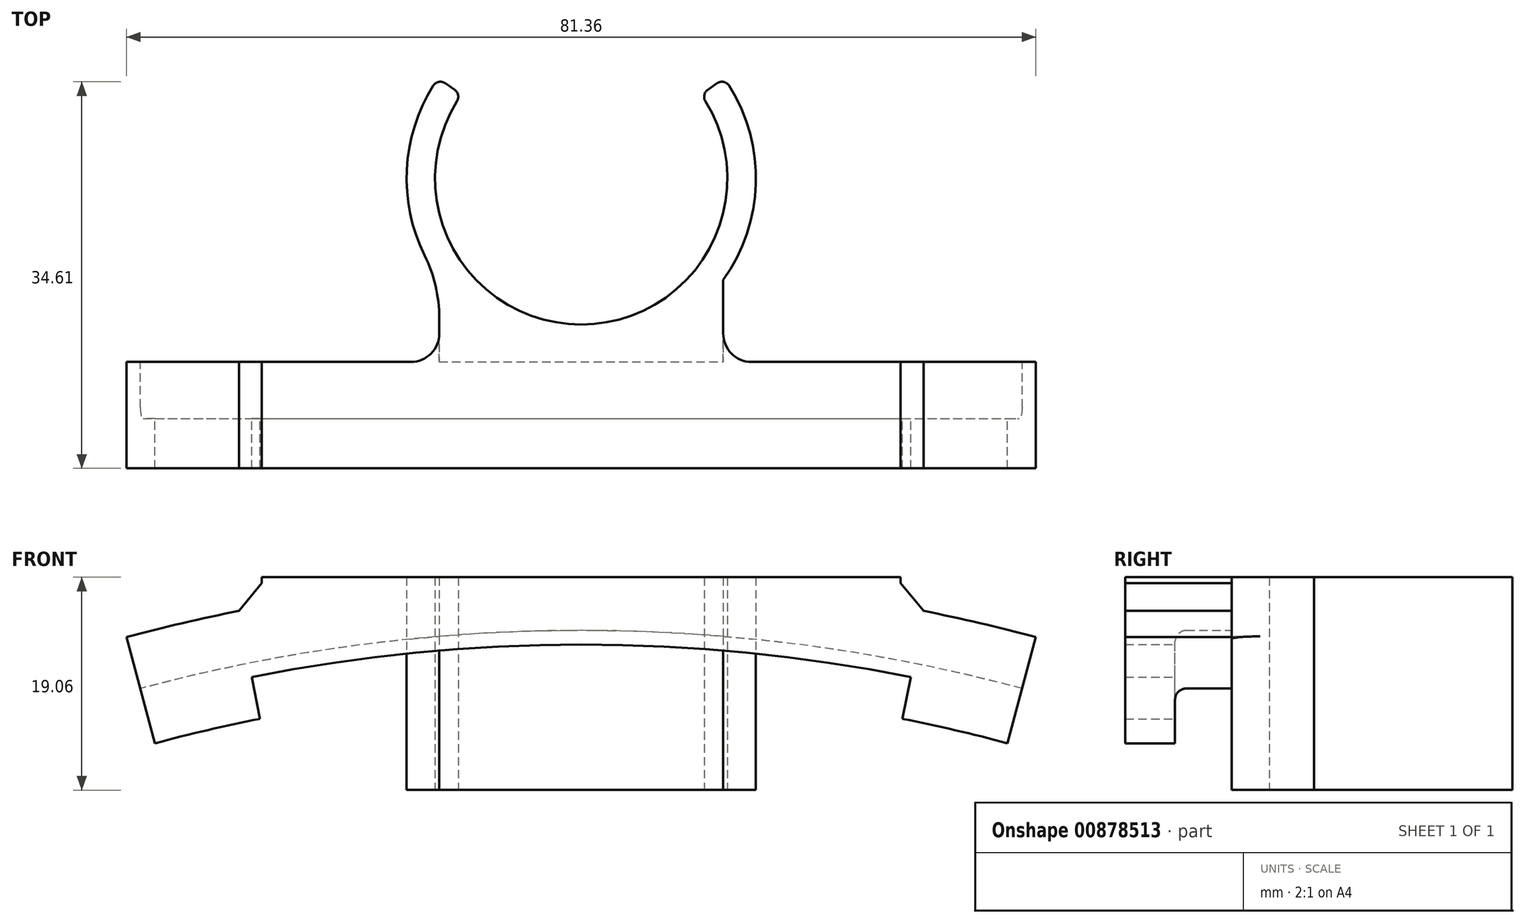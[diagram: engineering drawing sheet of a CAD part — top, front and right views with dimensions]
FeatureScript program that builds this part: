
annotation { "Feature Type Name" : "Feature", "Feature Type Description" : "" }
export const myFeature = defineFeature(function(context is Context, id is Id, definition is map)
    precondition{}
    {
        {
            var Q0;
            Q0=qCreatedBy(makeId("Top.planeOp"),FACE);
            var sketch = newSketch(context, id + "F0", { "sketchPlane" : qUnion([Q0])});
            skCircle(sketch, "E0", {"center": v(0, 0) * mm, "radius": 15.62 * mm});
            skCircle(sketch, "E1", {"center": v(0, 0) * mm, "radius": 13.08 * mm});
            skLineSegment(sketch, "E2", {"start": v(-53.94, 0) * mm, "end": v(51.47, 0) * mm, "construction": true});
            skLineSegment(sketch, "E3", {"start": v(0, 37.95) * mm, "end": v(0, -48.77) * mm, "construction": true});
            skLineSegment(sketch, "E4", {"start": v(0, 0) * mm, "end": v(-12.8, 8.96) * mm});
            skLineSegment(sketch, "E5.MirrorCS", {"start": v(0, 0) * mm, "end": v(12.8, 8.96) * mm});
            skLineSegment(sketch, "E6.top", {"start": v(-12.7, -16.43) * mm, "end": v(12.7, -16.43) * mm});
            skLineSegment(sketch, "E6.left", {"start": v(-12.7, -9.1) * mm, "end": v(-12.7, -16.43) * mm});
            skLineSegment(sketch, "E6.right", {"start": v(12.7, -9.1) * mm, "end": v(12.7, -16.43) * mm});
            skPoint(sketch, "E6.middle", {"position": v(0, -12.76) * mm});
            skCircle(sketch, "E7", {"center": v(0, 0) * mm, "radius": 13.34 * mm, "construction": true});
            skSolve(sketch);
        }
        {
            var Q0;
            {var subQ0=sQuery(id+"F0.wireOp",EDGE,"E4");var subQ5=sQuery(id+"F0.wireOp",EDGE,"E0");var subQ9=makeQuery(id+"F0.imprint","INTERSECT",VERTEX,{"derivedFrom":[subQ5,subQ0]});Q0=makeQuery(id+"F0.imprint","IMPRINT",FACE,{"disambiguationData":[TD([[makeQuery(id+"F0.imprint","IMPRINT",EDGE,{"disambiguationData":[TD([[subQ9,-1.0]])],"derivedFrom":subQ5}),1.0]])]});}
            extrude(context, id + "F1", {"entities" : qUnion([Q0]), "endBound" : BoundingType.SYMMETRIC, "depth" : 19.05 * mm, "offsetDistance" : 25.4 * mm});
        }
        {
            var Q0;
            Q0=makeQuery(id+"F0.imprint","IMPRINT",FACE,{"disambiguationData":[TD([[makeQuery(id+"F0.imprint","IMPRINT",EDGE,{"derivedFrom":sQuery(id+"F0.wireOp",EDGE,"E6.top")}),1.0]])]});
            extrude(context, id + "F2", {"entities" : qUnion([Q0]), "operationType" : NewBodyOperationType.ADD, "endBound" : BoundingType.SYMMETRIC, "depth" : 19.05 * mm, "offsetDistance" : 25.4 * mm});
        }
        {
            var Q0;
            Q0=makeQuery(id+"F2.opExtrude","SWEPT_EDGE",EDGE,{"disambiguationData":[OSD([sQuery(id+"F0.wireOp",EDGE,"E0"),sQuery(id+"F0.wireOp",EDGE,"E6.left")])]});
            var Q1;
            Q1=makeQuery(id+"F2.opExtrude","SWEPT_EDGE",EDGE,{"disambiguationData":[OSD([sQuery(id+"F0.wireOp",EDGE,"E0"),sQuery(id+"F0.wireOp",EDGE,"E6.right")])]});
            fillet(context, id + "F3", {"entities" : qUnion([Q0, Q1]), "radius" : 12.7 * mm, "tangentPropagation" : true, "allowEdgeOverflow" : false});
        }
        {
            var Q0;
            Q0=makeQuery(id+"F1.opExtrude","SWEPT_EDGE",EDGE,{"disambiguationData":[OSD([sQuery(id+"F0.wireOp",EDGE,"E0"),sQuery(id+"F0.wireOp",EDGE,"E4")])]});
            var Q1;
            Q1=makeQuery(id+"F1.opExtrude","SWEPT_EDGE",EDGE,{"disambiguationData":[OSD([sQuery(id+"F0.wireOp",EDGE,"E1"),sQuery(id+"F0.wireOp",EDGE,"E4")])]});
            var Q2;
            Q2=makeQuery(id+"F1.opExtrude","SWEPT_EDGE",EDGE,{"disambiguationData":[OSD([sQuery(id+"F0.wireOp",EDGE,"E0"),sQuery(id+"F0.wireOp",EDGE,"E5.MirrorCS")])]});
            var Q3;
            Q3=makeQuery(id+"F1.opExtrude","SWEPT_EDGE",EDGE,{"disambiguationData":[OSD([sQuery(id+"F0.wireOp",EDGE,"E1"),sQuery(id+"F0.wireOp",EDGE,"E5.MirrorCS")])]});
            fillet(context, id + "F4", {"entities" : qUnion([Q0, Q1, Q2, Q3]), "radius" : 0.76 * mm, "tangentPropagation" : true, "allowEdgeOverflow" : false});
        }
        {
            var Q0;
            Q0=makeQuery(id+"F2.opExtrude","SWEPT_FACE",FACE,{"disambiguationData":[OSD([sQuery(id+"F0.wireOp",EDGE,"E6.top")])]});
            var sketch = newSketch(context, id + "F5", { "sketchPlane" : qUnion([Q0])});
            skLineSegment(sketch, "E8", {"start": v(0, 225.36) * mm, "end": v(0, -360.44) * mm, "construction": true});
            skLineSegment(sketch, "E9", {"start": v(149.78, 4.76) * mm, "end": v(-228.02, 4.76) * mm, "construction": true});
            skCircle(sketch, "E10", {"center": v(0, -147.64) * mm, "radius": 152.4 * mm});
            skSolve(sketch);
        }
        {
            var Q0;
            Q0=qCreatedBy(makeId("Right.planeOp"),FACE);
            var sketch = newSketch(context, id + "F6", { "sketchPlane" : qUnion([Q0])});
            skLineSegment(sketch, "E11", {"start": v(-16.43, 9.53) * mm, "end": v(-25.96, 9.53) * mm});
            skLineSegment(sketch, "E12", {"start": v(-25.96, 9.53) * mm, "end": v(-25.96, -0.32) * mm});
            skLineSegment(sketch, "E13", {"start": v(-25.96, -0.32) * mm, "end": v(-21.51, -0.32) * mm});
            skLineSegment(sketch, "E14", {"start": v(-21.51, -0.32) * mm, "end": v(-21.51, 4.76) * mm});
            skLineSegment(sketch, "E15", {"start": v(-21.51, 4.76) * mm, "end": v(-16.43, 4.76) * mm});
            skLineSegment(sketch, "E16", {"start": v(-16.43, 4.76) * mm, "end": v(-16.43, 9.53) * mm});
            skLineSegment(sketch, "E17.top", {"start": v(-16.43, 5.72) * mm, "end": v(-25.96, 5.71) * mm});
            skLineSegment(sketch, "E17.left", {"start": v(-16.43, 9.53) * mm, "end": v(-16.43, 5.72) * mm});
            skLineSegment(sketch, "E17.right", {"start": v(-25.96, 9.53) * mm, "end": v(-25.96, 5.71) * mm});
            skLineSegment(sketch, "E18.top", {"start": v(-25.96, 3.5) * mm, "end": v(-21.51, 3.5) * mm});
            skLineSegment(sketch, "E18.left", {"start": v(-25.96, -0.32) * mm, "end": v(-25.96, 3.5) * mm});
            skLineSegment(sketch, "E18.right", {"start": v(-21.51, -0.32) * mm, "end": v(-21.51, 3.5) * mm});
            skSolve(sketch);
        }
        {
            var Q0;
            Q0 = qSketchRegion(id + "F6", true);
            var Q1;
            Q1=sQuery(id+"F5.wireOp",EDGE,"E10");
            revolve(context, id + "F7", {"operationType" : NewBodyOperationType.ADD, "surfaceOperationType" : NewSurfaceOperationType.NEW, "entities" : qUnion([Q0]), "axis" : qUnion([Q1]), "revolveType" : RevolveType.SYMMETRIC, "angle" : 30 * degree});
        }
        {
            var Q0;
            Q0=makeQuery(id+"F7.opRevolve","SWEPT_EDGE",EDGE,{"disambiguationData":[OSD([sQuery(id+"F6.wireOp",EDGE,"E14"),sQuery(id+"F6.wireOp",EDGE,"E15")])]});
            fillet(context, id + "F8", {"entities" : qUnion([Q0]), "tangentPropagation" : true, "radius" : 1.02 * mm, "defaultsChanged" : true, "vertexSettings" : [], "allowEdgeOverflow" : false});
        }
        {
            var Q0;
            Q0 = qSketchRegion(id + "F6", true);
            extrude(context, id + "F9", {"entities" : qUnion([Q0]), "operationType" : NewBodyOperationType.ADD, "endBound" : BoundingType.SYMMETRIC, "depth" : 57.15 * mm, "offsetDistance" : 25.4 * mm});
        }
        {
            var Q0;
            {var subQ0=sQuery(id+"F0.wireOp",EDGE,"E6.left");var subQ1=makeQuery(id+"F2.opExtrude","SWEPT_FACE",FACE,{"disambiguationData":[OSD([subQ0])]});var subQ2=makeQuery(id+"F7.opRevolve","SWEPT_FACE",FACE,{"disambiguationData":[OSD([sQuery(id+"F6.wireOp",EDGE,"E16")])]});var subQ3=sQuery(id+"F0.wireOp",EDGE,"E6.top");var subQ4=makeQuery(id+"F2.opExtrude","SWEPT_EDGE",EDGE,{"disambiguationData":[OSD([subQ3,subQ0])]});var subQ5=makeQuery(id+"F2.opExtrude","SWEPT_FACE",FACE,{"disambiguationData":[OSD([subQ3])]});Q0=makeQuery(id+"F9.boolean.opBoolean","MERGE",EDGE,{"derivedFrom":[makeQuery(id+"F7.boolean.opBoolean","SPLIT",EDGE,{"disambiguationData":[topologyDisambiguationEdgeConnected([subQ5,subQ1]),TD([makeQuery(id+"F7.opRevolve","SWEPT_FACE",FACE,{"disambiguationData":[OSD([sQuery(id+"F6.wireOp",EDGE,"E11")])]})])],"derivedFrom":subQ4}),makeQuery(id+"F7.boolean.opBoolean","SPLIT",EDGE,{"disambiguationData":[topologyDisambiguationEdgeConnected([subQ1,subQ2])],"derivedFrom":subQ4})]});}
            var Q1;
            {var subQ0=sQuery(id+"F0.wireOp",EDGE,"E6.right");var subQ1=makeQuery(id+"F2.opExtrude","SWEPT_FACE",FACE,{"disambiguationData":[OSD([subQ0])]});var subQ2=makeQuery(id+"F7.opRevolve","SWEPT_FACE",FACE,{"disambiguationData":[OSD([sQuery(id+"F6.wireOp",EDGE,"E16")])]});var subQ3=sQuery(id+"F0.wireOp",EDGE,"E6.top");var subQ4=makeQuery(id+"F2.opExtrude","SWEPT_EDGE",EDGE,{"disambiguationData":[OSD([subQ3,subQ0])]});var subQ5=makeQuery(id+"F2.opExtrude","SWEPT_FACE",FACE,{"disambiguationData":[OSD([subQ3])]});Q1=makeQuery(id+"F9.boolean.opBoolean","MERGE",EDGE,{"derivedFrom":[makeQuery(id+"F7.boolean.opBoolean","SPLIT",EDGE,{"disambiguationData":[topologyDisambiguationEdgeConnected([subQ5,subQ1]),TD([makeQuery(id+"F7.opRevolve","SWEPT_FACE",FACE,{"disambiguationData":[OSD([sQuery(id+"F6.wireOp",EDGE,"E11")])]})])],"derivedFrom":subQ4}),makeQuery(id+"F7.boolean.opBoolean","SPLIT",EDGE,{"disambiguationData":[topologyDisambiguationEdgeConnected([subQ1,subQ2])],"derivedFrom":subQ4})]});}
            fillet(context, id + "F10", {"entities" : qUnion([Q0, Q1]), "tangentPropagation" : true, "radius" : 2.54 * mm, "defaultsChanged" : false, "vertexSettings" : [], "allowEdgeOverflow" : false});
        }
        {
            var Q0;
            {var subQ0=sQuery(id+"F6.wireOp",EDGE,"E11");Q0=makeQuery(id+"F9.boolean.opBoolean","INTERSECT",EDGE,{"derivedFrom":[makeQuery(id+"F7.opRevolve","SWEPT_FACE",FACE,{"disambiguationData":[OSD([subQ0])]}),makeQuery(id+"F9.opExtrude","CAP_FACE",FACE,{"disambiguationData":[OSD([subQ0,sQuery(id+"F6.wireOp",EDGE,"E12"),sQuery(id+"F6.wireOp",EDGE,"E13"),sQuery(id+"F6.wireOp",EDGE,"E14"),sQuery(id+"F6.wireOp",EDGE,"E15"),sQuery(id+"F6.wireOp",EDGE,"E16")])],"isStart":true})]});}
            var Q1;
            {var subQ0=sQuery(id+"F6.wireOp",EDGE,"E11");Q1=makeQuery(id+"F9.boolean.opBoolean","INTERSECT",EDGE,{"derivedFrom":[makeQuery(id+"F7.opRevolve","SWEPT_FACE",FACE,{"disambiguationData":[OSD([subQ0])]}),makeQuery(id+"F9.opExtrude","CAP_FACE",FACE,{"disambiguationData":[OSD([subQ0,sQuery(id+"F6.wireOp",EDGE,"E12"),sQuery(id+"F6.wireOp",EDGE,"E13"),sQuery(id+"F6.wireOp",EDGE,"E14"),sQuery(id+"F6.wireOp",EDGE,"E15"),sQuery(id+"F6.wireOp",EDGE,"E16")])],"isStart":false})]});}
            chamfer(context, id + "F11", {"entities" : qUnion([Q0, Q1]), "width" : 2.54 * mm, "tangentPropagation" : true});
        }
        {
            var Q0;
            {var subQ2=sQuery(id+"F6.wireOp",EDGE,"E13");Q0=makeQuery(id+"F6.imprint","IMPRINT",FACE,{"disambiguationData":[TD([[makeQuery(id+"F6.imprint","IMPRINT",EDGE,{"derivedFrom":subQ2}),1.0]])]});}
            var Q1;
            Q1=makeQuery(id+"F7.opRevolve","SWEPT_EDGE",EDGE,{"disambiguationData":[OSD([sQuery(id+"F6.wireOp",EDGE,"E12"),sQuery(id+"F6.wireOp",EDGE,"E13")])]});
            revolve(context, id + "F12", {"operationType" : NewBodyOperationType.REMOVE, "surfaceOperationType" : NewSurfaceOperationType.NEW, "entities" : qUnion([Q0]), "axis" : qUnion([Q1]), "revolveType" : RevolveType.SYMMETRIC, "oppositeDirection" : true, "angle" : 22.5 * degree});
        }
    });
